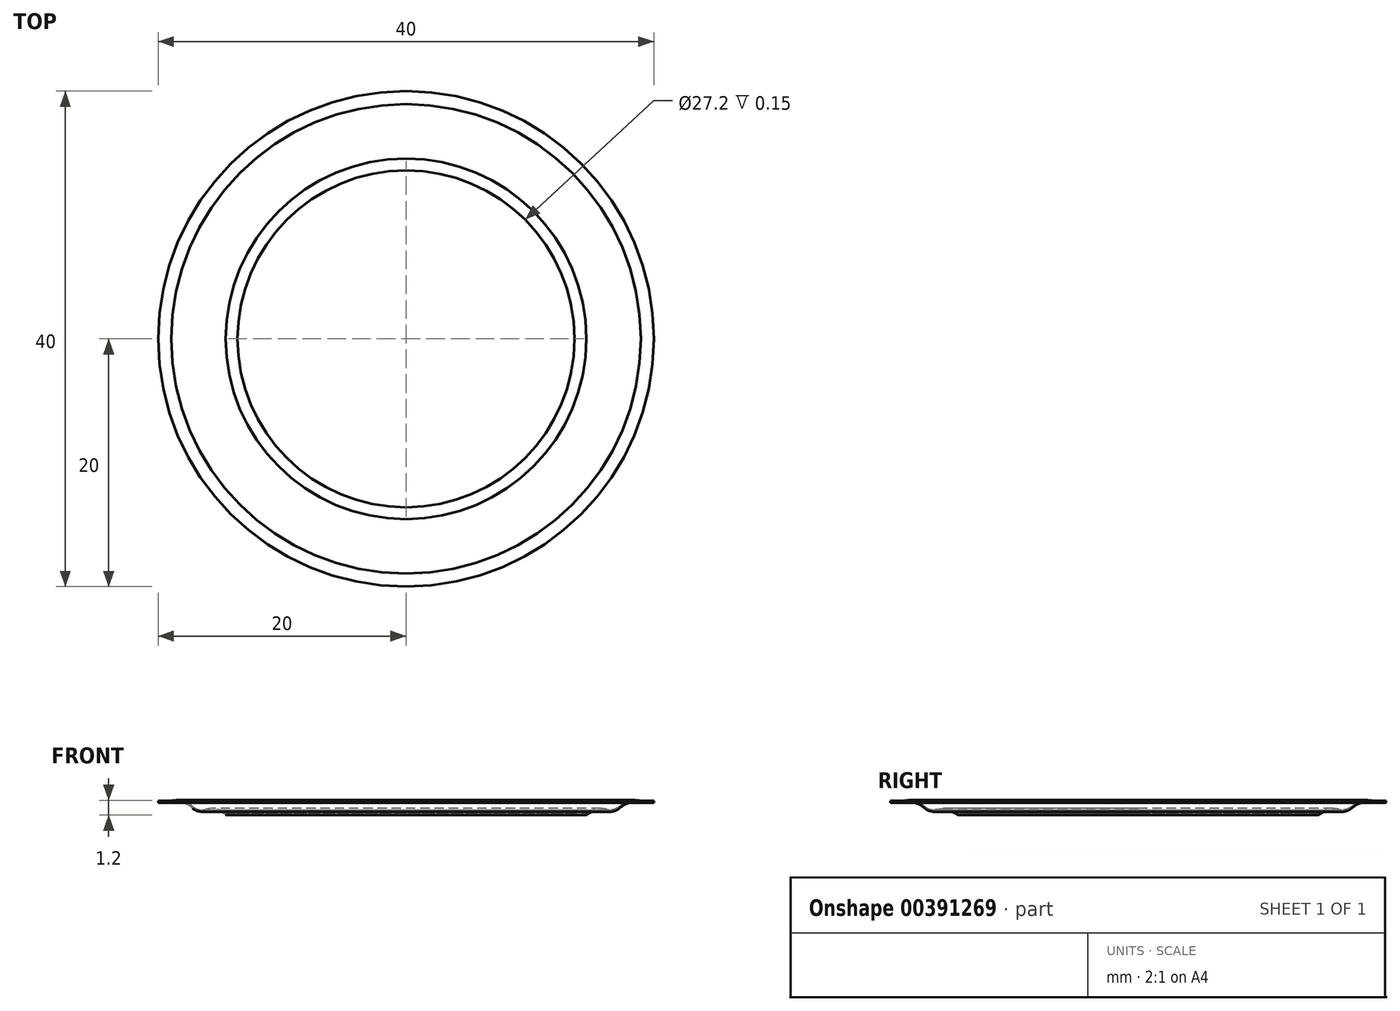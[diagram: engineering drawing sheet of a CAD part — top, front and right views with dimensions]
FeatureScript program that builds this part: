
annotation { "Feature Type Name" : "Feature", "Feature Type Description" : "" }
export const myFeature = defineFeature(function(context is Context, id is Id, definition is map)
    precondition{}
    {
        {
            var Q0;
            Q0=qCreatedBy(makeId("Front.planeOp"),FACE);
            var sketch = newSketch(context, id + "F0", { "sketchPlane" : qUnion([Q0])});
            skLineSegment(sketch, "E0", {"start": v(0, 0) * mm, "end": v(0.96, 0) * mm});
            skArc(sketch, "E1", {"start": v(2.62, 0.32) * mm, "mid": v(1.75, 0.35) * mm, "end": v(0.96, 0) * mm});
            skPoint(sketch, "E1.third.point", {"position": v(3.86, -2.26) * mm});
            skLineSegment(sketch, "E2", {"start": v(6.4, 1) * mm, "end": v(5.36, 1) * mm});
            skArc(sketch, "E3", {"start": v(5.36, 1) * mm, "mid": v(4.45, 1) * mm, "end": v(3.64, 0.56) * mm});
            skPoint(sketch, "E3.third.point", {"position": v(5.56, -2.64) * mm});
            skArc(sketch, "E4", {"start": v(2.61, 0.32) * mm, "mid": v(3.16, 0.3) * mm, "end": v(3.65, 0.57) * mm});
            skPoint(sketch, "E4.third.point", {"position": v(2.76, 2.47) * mm});
            skLineSegment(sketch, "E5.trimOffspring", {"start": v(5.36, 1) * mm, "end": v(6.4, 1) * mm});
            skPoint(sketch, "E6.start.orphan", {"position": v(0.96, 1) * mm});
            skPoint(sketch, "E7.start.orphan", {"position": v(2.6, 1) * mm});
            skLineSegment(sketch, "E8", {"start": v(0.96, 0) * mm, "end": v(0.01, 0) * mm});
            skLineSegment(sketch, "E9", {"start": v(-13.59, 0) * mm, "end": v(-13.59, 12.35) * mm});
            skLineSegment(sketch, "E10", {"start": v(0.01, 0) * mm, "end": v(0.01, -0.15) * mm});
            skLineSegment(sketch, "E11", {"start": v(0.01, -0.15) * mm, "end": v(0.96, -0.15) * mm});
            skArc(sketch, "E12", {"start": v(2.62, 0.17) * mm, "mid": v(1.75, 0.2) * mm, "end": v(0.96, -0.15) * mm});
            skArc(sketch, "E13", {"start": v(5.36, 0.85) * mm, "mid": v(4.45, 0.84) * mm, "end": v(3.64, 0.41) * mm});
            skArc(sketch, "E14", {"start": v(2.61, 0.17) * mm, "mid": v(3.16, 0.16) * mm, "end": v(3.65, 0.42) * mm});
            skLineSegment(sketch, "E15.trimOffspring", {"start": v(5.36, 0.85) * mm, "end": v(6.4, 0.85) * mm});
            skLineSegment(sketch, "E16", {"start": v(6.4, 0.85) * mm, "end": v(6.4, 1) * mm});
            skSolve(sketch);
        }
        {
            var Q0;
            {var subQ3=sQuery(id+"F0.wireOp",EDGE,"E1");Q0=makeQuery(id+"F0.imprint","IMPRINT",FACE,{"disambiguationData":[TD([[makeQuery(id+"F0.imprint","IMPRINT",EDGE,{"derivedFrom":subQ3}),1.0]])]});}
            var Q1;
            Q1=sQuery(id+"F0.wireOp",EDGE,"E9");
            revolve(context, id + "F1", {"entities" : qUnion([Q0]), "axis" : qUnion([Q1]), "revolveType" : RevolveType.FULL});
        }
    });
